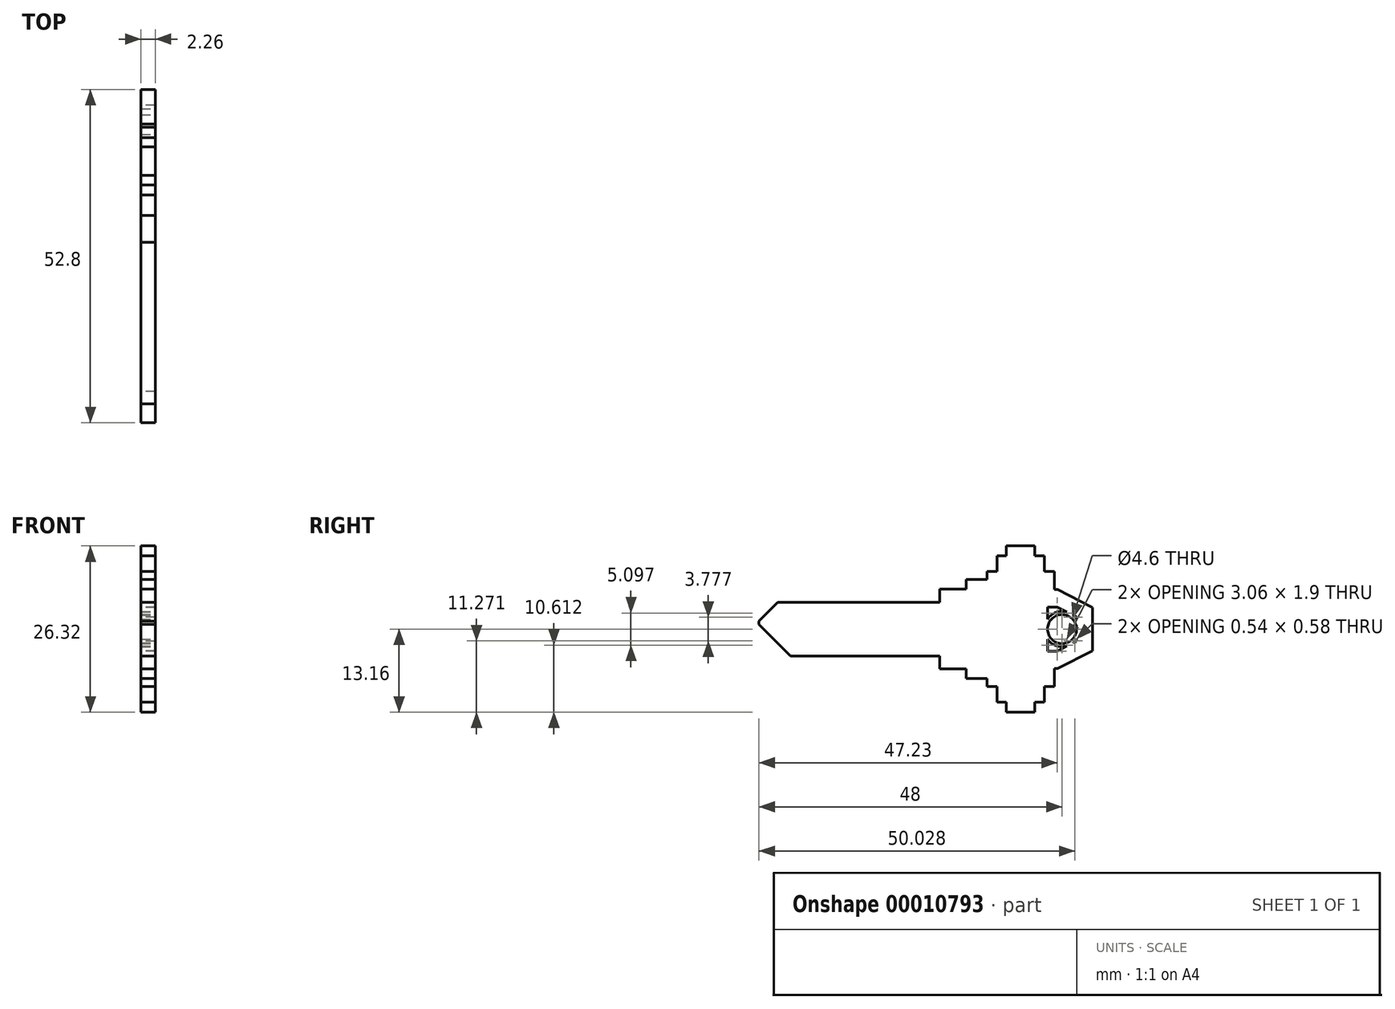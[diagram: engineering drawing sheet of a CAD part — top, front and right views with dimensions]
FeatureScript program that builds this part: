
annotation { "Feature Type Name" : "Feature", "Feature Type Description" : "" }
export const myFeature = defineFeature(function(context is Context, id is Id, definition is map)
    precondition{}
    {
        {
            var Q0;
            Q0=qCreatedBy(makeId("Right.planeOp"),FACE);
            var sketch = newSketch(context, id + "F0", { "sketchPlane" : qUnion([Q0])});
            skLineSegment(sketch, "E0", {"start": v(-2.3, 3.5) * mm, "end": v(-2.3, -3.5) * mm});
            skLineSegment(sketch, "E1", {"start": v(-2.3, -3.5) * mm, "end": v(-0.8, -3.5) * mm});
            skLineSegment(sketch, "E2", {"start": v(-0.8, -3.5) * mm, "end": v(2.3, -1.9) * mm});
            skLineSegment(sketch, "E3", {"start": v(2.3, -1.9) * mm, "end": v(2.3, 1.9) * mm});
            skLineSegment(sketch, "E4", {"start": v(2.3, 1.9) * mm, "end": v(-0.8, 3.5) * mm});
            skLineSegment(sketch, "E5", {"start": v(-0.8, 3.5) * mm, "end": v(-2.3, 3.5) * mm});
            skLineSegment(sketch, "E6", {"start": v(0, 0) * mm, "end": v(-15.57, 0) * mm, "construction": true});
            skCircle(sketch, "E7", {"center": v(0, 0) * mm, "radius": 2.3 * mm, "construction": true});
            skLineSegment(sketch, "E8", {"start": v(-0.68, 6.25) * mm, "end": v(4.8, 3.42) * mm});
            skLineSegment(sketch, "E9", {"start": v(4.8, 3.42) * mm, "end": v(4.8, -3.42) * mm});
            skLineSegment(sketch, "E10", {"start": v(4.8, -3.42) * mm, "end": v(-0.68, -6.25) * mm});
            skLineSegment(sketch, "E11", {"start": v(-0.68, 6.25) * mm, "end": v(-1.2, 6.25) * mm});
            skLineSegment(sketch, "E12", {"start": v(-1.2, 6.25) * mm, "end": v(-1.2, 9.13) * mm});
            skLineSegment(sketch, "E13", {"start": v(-1.2, 9.13) * mm, "end": v(-2.8, 9.13) * mm});
            skLineSegment(sketch, "E14", {"start": v(-2.8, 9.13) * mm, "end": v(-2.8, 11.58) * mm});
            skLineSegment(sketch, "E15", {"start": v(-2.8, 11.58) * mm, "end": v(-4.3, 11.58) * mm});
            skLineSegment(sketch, "E16", {"start": v(-4.3, 11.58) * mm, "end": v(-4.3, 13.16) * mm});
            skLineSegment(sketch, "E17", {"start": v(-4.3, 13.16) * mm, "end": v(-8.8, 13.16) * mm});
            skLineSegment(sketch, "E18", {"start": v(-8.8, 13.16) * mm, "end": v(-8.8, 11.58) * mm});
            skLineSegment(sketch, "E19", {"start": v(-8.8, 11.58) * mm, "end": v(-10.3, 11.58) * mm});
            skLineSegment(sketch, "E20", {"start": v(-10.3, 11.57) * mm, "end": v(-10.3, 9.12) * mm});
            skLineSegment(sketch, "E21", {"start": v(-10.3, 9.12) * mm, "end": v(-11.9, 9.12) * mm});
            skLineSegment(sketch, "E22", {"start": v(-11.9, 9.12) * mm, "end": v(-11.9, 7.85) * mm});
            skLineSegment(sketch, "E23", {"start": v(-11.9, 7.85) * mm, "end": v(-15.15, 7.85) * mm});
            skLineSegment(sketch, "E24", {"start": v(-15.15, 7.85) * mm, "end": v(-15.15, 6.3) * mm});
            skLineSegment(sketch, "E25", {"start": v(-15.15, 6.3) * mm, "end": v(-19.4, 6.3) * mm});
            skLineSegment(sketch, "E26", {"start": v(-19.4, 6.3) * mm, "end": v(-19.4, 4.25) * mm});
            skLineSegment(sketch, "E27", {"start": v(-19.4, 4.25) * mm, "end": v(-48, 4.25) * mm});
            skLineSegment(sketch, "E28", {"start": v(-48, 4.25) * mm, "end": v(-48, -4.25) * mm});
            skLineSegment(sketch, "E29.0.MirrorCS", {"start": v(-0.68, -6.25) * mm, "end": v(-1.2, -6.25) * mm});
            skLineSegment(sketch, "E30.0.MirrorCS", {"start": v(-1.2, -6.25) * mm, "end": v(-1.2, -9.13) * mm});
            skLineSegment(sketch, "E31.0.MirrorCS", {"start": v(-1.2, -9.13) * mm, "end": v(-2.8, -9.13) * mm});
            skLineSegment(sketch, "E32.0.MirrorCS", {"start": v(-2.8, -9.13) * mm, "end": v(-2.8, -11.58) * mm});
            skLineSegment(sketch, "E33.0.MirrorCS", {"start": v(-2.8, -11.58) * mm, "end": v(-4.3, -11.58) * mm});
            skLineSegment(sketch, "E34.0.MirrorCS", {"start": v(-4.3, -11.58) * mm, "end": v(-4.3, -13.16) * mm});
            skLineSegment(sketch, "E35.0.MirrorCS", {"start": v(-4.3, -13.16) * mm, "end": v(-8.8, -13.16) * mm});
            skLineSegment(sketch, "E36.0.MirrorCS", {"start": v(-8.8, -13.16) * mm, "end": v(-8.8, -11.58) * mm});
            skLineSegment(sketch, "E37.0.MirrorCS", {"start": v(-8.8, -11.58) * mm, "end": v(-10.3, -11.58) * mm});
            skLineSegment(sketch, "E38.0.MirrorCS", {"start": v(-10.3, -11.58) * mm, "end": v(-10.3, -9.13) * mm});
            skLineSegment(sketch, "E39.0.MirrorCS", {"start": v(-10.3, -9.13) * mm, "end": v(-11.9, -9.13) * mm});
            skLineSegment(sketch, "E40.0.MirrorCS", {"start": v(-11.9, -9.13) * mm, "end": v(-11.9, -7.85) * mm});
            skLineSegment(sketch, "E41.0.MirrorCS", {"start": v(-11.9, -7.85) * mm, "end": v(-15.15, -7.85) * mm});
            skLineSegment(sketch, "E42.0.MirrorCS", {"start": v(-15.15, -7.85) * mm, "end": v(-15.15, -6.3) * mm});
            skLineSegment(sketch, "E43.0.MirrorCS", {"start": v(-15.15, -6.3) * mm, "end": v(-19.4, -6.3) * mm});
            skLineSegment(sketch, "E44.0.MirrorCS", {"start": v(-19.4, -6.3) * mm, "end": v(-19.4, -4.25) * mm});
            skLineSegment(sketch, "E45.0.MirrorCS", {"start": v(-19.4, -4.25) * mm, "end": v(-48, -4.25) * mm});
            skLineSegment(sketch, "E46", {"start": v(-6.55, 13.16) * mm, "end": v(-6.55, -13.16) * mm, "construction": true});
            skSolve(sketch);
        }
        {
            var Q0;
            Q0 = qSketchRegion(id + "F0", true);
            extrude(context, id + "F1", {"entities" : qUnion([Q0]), "depth" : 2.25 * mm, "symmetric" : true});
        }
        {
            var Q0;
            Q0=makeQuery(id+"F1.opExtrude","CAP_FACE",FACE,{"disambiguationData":[OSD([sQuery(id+"F0.wireOp",EDGE,"E0"),sQuery(id+"F0.wireOp",EDGE,"E1"),sQuery(id+"F0.wireOp",EDGE,"E2"),sQuery(id+"F0.wireOp",EDGE,"E3"),sQuery(id+"F0.wireOp",EDGE,"E4"),sQuery(id+"F0.wireOp",EDGE,"E5"),sQuery(id+"F0.wireOp",EDGE,"E8"),sQuery(id+"F0.wireOp",EDGE,"E9"),sQuery(id+"F0.wireOp",EDGE,"E10"),sQuery(id+"F0.wireOp",EDGE,"E11"),sQuery(id+"F0.wireOp",EDGE,"E12"),sQuery(id+"F0.wireOp",EDGE,"E13"),sQuery(id+"F0.wireOp",EDGE,"E14"),sQuery(id+"F0.wireOp",EDGE,"E15"),sQuery(id+"F0.wireOp",EDGE,"E16"),sQuery(id+"F0.wireOp",EDGE,"E17"),sQuery(id+"F0.wireOp",EDGE,"E18"),sQuery(id+"F0.wireOp",EDGE,"E19"),sQuery(id+"F0.wireOp",EDGE,"E20"),sQuery(id+"F0.wireOp",EDGE,"E21"),sQuery(id+"F0.wireOp",EDGE,"E22"),sQuery(id+"F0.wireOp",EDGE,"E23"),sQuery(id+"F0.wireOp",EDGE,"E24"),sQuery(id+"F0.wireOp",EDGE,"E25"),sQuery(id+"F0.wireOp",EDGE,"E26"),sQuery(id+"F0.wireOp",EDGE,"E27"),sQuery(id+"F0.wireOp",EDGE,"E28"),sQuery(id+"F0.wireOp",EDGE,"E29.0.MirrorCS"),sQuery(id+"F0.wireOp",EDGE,"E30.0.MirrorCS"),sQuery(id+"F0.wireOp",EDGE,"E31.0.MirrorCS"),sQuery(id+"F0.wireOp",EDGE,"E32.0.MirrorCS"),sQuery(id+"F0.wireOp",EDGE,"E33.0.MirrorCS"),sQuery(id+"F0.wireOp",EDGE,"E34.0.MirrorCS"),sQuery(id+"F0.wireOp",EDGE,"E35.0.MirrorCS"),sQuery(id+"F0.wireOp",EDGE,"E36.0.MirrorCS"),sQuery(id+"F0.wireOp",EDGE,"E37.0.MirrorCS"),sQuery(id+"F0.wireOp",EDGE,"E38.0.MirrorCS"),sQuery(id+"F0.wireOp",EDGE,"E39.0.MirrorCS"),sQuery(id+"F0.wireOp",EDGE,"E40.0.MirrorCS"),sQuery(id+"F0.wireOp",EDGE,"E41.0.MirrorCS"),sQuery(id+"F0.wireOp",EDGE,"E42.0.MirrorCS"),sQuery(id+"F0.wireOp",EDGE,"E43.0.MirrorCS"),sQuery(id+"F0.wireOp",EDGE,"E44.0.MirrorCS"),sQuery(id+"F0.wireOp",EDGE,"E45.0.MirrorCS")])],"isStart":false});
            var sketch = newSketch(context, id + "F2", { "sketchPlane" : qUnion([Q0])});
            skCircle(sketch, "E47.0", {"center": v(0, 0) * mm, "radius": 2.3 * mm});
            skCircle(sketch, "E48", {"center": v(0, 0) * mm, "radius": 2.8 * mm});
            skSolve(sketch);
        }
        {
            var Q0;
            Q0 = qSketchRegion(id + "F2", true);
            var Q1;
            Q1=makeQuery(id+"F1.opExtrude","CAP_FACE",FACE,{"disambiguationData":[OSD([sQuery(id+"F0.wireOp",EDGE,"E0"),sQuery(id+"F0.wireOp",EDGE,"E1"),sQuery(id+"F0.wireOp",EDGE,"E2"),sQuery(id+"F0.wireOp",EDGE,"E3"),sQuery(id+"F0.wireOp",EDGE,"E4"),sQuery(id+"F0.wireOp",EDGE,"E5"),sQuery(id+"F0.wireOp",EDGE,"E8"),sQuery(id+"F0.wireOp",EDGE,"E9"),sQuery(id+"F0.wireOp",EDGE,"E10"),sQuery(id+"F0.wireOp",EDGE,"E11"),sQuery(id+"F0.wireOp",EDGE,"E12"),sQuery(id+"F0.wireOp",EDGE,"E13"),sQuery(id+"F0.wireOp",EDGE,"E14"),sQuery(id+"F0.wireOp",EDGE,"E15"),sQuery(id+"F0.wireOp",EDGE,"E16"),sQuery(id+"F0.wireOp",EDGE,"E17"),sQuery(id+"F0.wireOp",EDGE,"E18"),sQuery(id+"F0.wireOp",EDGE,"E19"),sQuery(id+"F0.wireOp",EDGE,"E20"),sQuery(id+"F0.wireOp",EDGE,"E21"),sQuery(id+"F0.wireOp",EDGE,"E22"),sQuery(id+"F0.wireOp",EDGE,"E23"),sQuery(id+"F0.wireOp",EDGE,"E24"),sQuery(id+"F0.wireOp",EDGE,"E25"),sQuery(id+"F0.wireOp",EDGE,"E26"),sQuery(id+"F0.wireOp",EDGE,"E27"),sQuery(id+"F0.wireOp",EDGE,"E28"),sQuery(id+"F0.wireOp",EDGE,"E29.0.MirrorCS"),sQuery(id+"F0.wireOp",EDGE,"E30.0.MirrorCS"),sQuery(id+"F0.wireOp",EDGE,"E31.0.MirrorCS"),sQuery(id+"F0.wireOp",EDGE,"E32.0.MirrorCS"),sQuery(id+"F0.wireOp",EDGE,"E33.0.MirrorCS"),sQuery(id+"F0.wireOp",EDGE,"E34.0.MirrorCS"),sQuery(id+"F0.wireOp",EDGE,"E35.0.MirrorCS"),sQuery(id+"F0.wireOp",EDGE,"E36.0.MirrorCS"),sQuery(id+"F0.wireOp",EDGE,"E37.0.MirrorCS"),sQuery(id+"F0.wireOp",EDGE,"E38.0.MirrorCS"),sQuery(id+"F0.wireOp",EDGE,"E39.0.MirrorCS"),sQuery(id+"F0.wireOp",EDGE,"E40.0.MirrorCS"),sQuery(id+"F0.wireOp",EDGE,"E41.0.MirrorCS"),sQuery(id+"F0.wireOp",EDGE,"E42.0.MirrorCS"),sQuery(id+"F0.wireOp",EDGE,"E43.0.MirrorCS"),sQuery(id+"F0.wireOp",EDGE,"E44.0.MirrorCS"),sQuery(id+"F0.wireOp",EDGE,"E45.0.MirrorCS")])],"isStart":true});
            extrude(context, id + "F3", {"entities" : qUnion([Q0]), "operationType" : NewBodyOperationType.ADD, "endBound" : BoundingType.UP_TO_SURFACE, "oppositeDirection" : true, "endBoundEntityFace" : qUnion([Q1]), "depth" : 25 * mm});
        }
        {
            var Q0;
            Q0=makeQuery(id+"F1.opExtrude","SWEPT_EDGE",EDGE,{"disambiguationData":[OSD([sQuery(id+"F0.wireOp",EDGE,"E27"),sQuery(id+"F0.wireOp",EDGE,"E28")])]});
            chamfer(context, id + "F4", {"entities" : qUnion([Q0]), "width" : 3 * mm, "tangentPropagation" : true});
        }
        {
            var Q0;
            Q0=makeQuery(id+"F1.opExtrude","SWEPT_EDGE",EDGE,{"disambiguationData":[OSD([sQuery(id+"F0.wireOp",EDGE,"E28"),sQuery(id+"F0.wireOp",EDGE,"E45.0.MirrorCS")])]});
            chamfer(context, id + "F5", {"entities" : qUnion([Q0]), "width" : 5 * mm, "tangentPropagation" : true});
        }
    });
